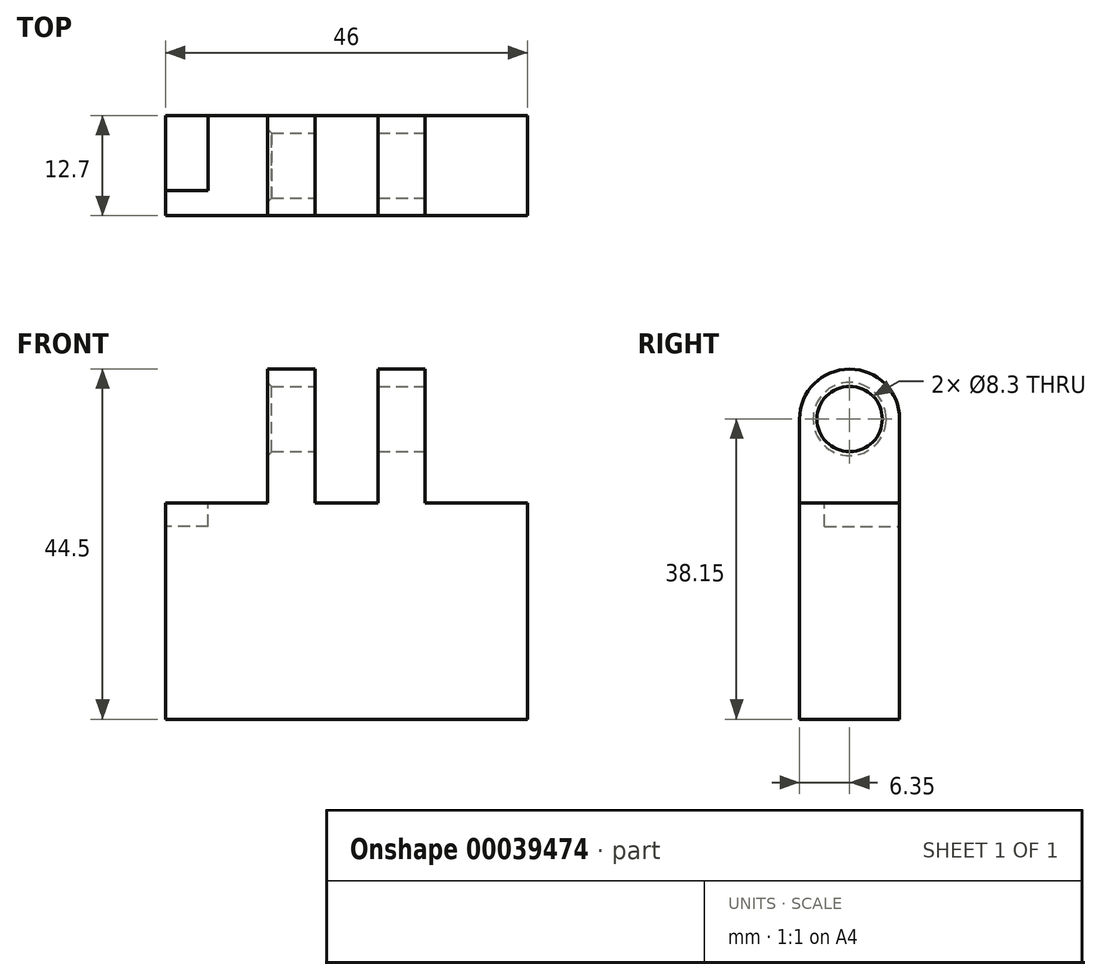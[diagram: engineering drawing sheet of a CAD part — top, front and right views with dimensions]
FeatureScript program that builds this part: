
annotation { "Feature Type Name" : "Feature", "Feature Type Description" : "" }
export const myFeature = defineFeature(function(context is Context, id is Id, definition is map)
    precondition{}
    {
        {
            var Q0;
            Q0=qCreatedBy(makeId("Top.planeOp"),FACE);
            var sketch = newSketch(context, id + "F0", { "sketchPlane" : qUnion([Q0])});
            skLineSegment(sketch, "E0.rect.bottom", {"start": v(23, -6.35) * mm, "end": v(-23, -6.35) * mm});
            skLineSegment(sketch, "E0.rect.top", {"start": v(23, 6.35) * mm, "end": v(-23, 6.35) * mm});
            skLineSegment(sketch, "E0.rect.left", {"start": v(23, -6.35) * mm, "end": v(23, 6.35) * mm});
            skLineSegment(sketch, "E0.rect.right", {"start": v(-23, -6.35) * mm, "end": v(-23, 6.35) * mm});
            skPoint(sketch, "E0.rect.middle", {"position": v(0, 0) * mm});
            skLineSegment(sketch, "E1", {"start": v(-23, 6.35) * mm, "end": v(23, 6.35) * mm});
            skLineSegment(sketch, "E2", {"start": v(-23, -3.2) * mm, "end": v(23, -3.2) * mm});
            skLineSegment(sketch, "E3", {"start": v(-17.6, 6.35) * mm, "end": v(-17.6, -6.35) * mm});
            skLineSegment(sketch, "E4", {"start": v(0, 15.39) * mm, "end": v(0, -22.17) * mm, "construction": true});
            skLineSegment(sketch, "E5.MirrorCS", {"start": v(17.6, 6.35) * mm, "end": v(17.6, -6.35) * mm});
            skLineSegment(sketch, "E6", {"start": v(-31.76, 0) * mm, "end": v(24.03, 0) * mm, "construction": true});
            skSolve(sketch);
        }
        {
            var Q0;
            {var subQ3=sQuery(id+"F0.wireOp",EDGE,"E1");var subQ5=sQuery(id+"F0.wireOp",EDGE,"E0.rect.right");var subQ7=makeQuery(id+"F0.imprint","INTERSECT",VERTEX,{"derivedFrom":[subQ5,subQ3]});Q0=makeQuery(id+"F0.imprint","IMPRINT",FACE,{"disambiguationData":[TD([[makeQuery(id+"F0.imprint","IMPRINT",EDGE,{"disambiguationData":[TD([[subQ7,1.0]])],"derivedFrom":subQ5}),-1.0]])]});}
            var Q1;
            {var subQ3=sQuery(id+"F0.wireOp",EDGE,"E1");var subQ5=sQuery(id+"F0.wireOp",EDGE,"E3");var subQ7=makeQuery(id+"F0.imprint","INTERSECT",VERTEX,{"derivedFrom":[subQ3,subQ5]});Q1=makeQuery(id+"F0.imprint","IMPRINT",FACE,{"disambiguationData":[TD([[makeQuery(id+"F0.imprint","IMPRINT",EDGE,{"disambiguationData":[TD([[subQ7,-1.0]])],"derivedFrom":subQ3}),-1.0]])]});}
            var Q2;
            {var subQ3=sQuery(id+"F0.wireOp",EDGE,"E0.rect.left");var subQ5=sQuery(id+"F0.wireOp",EDGE,"E1");var subQ7=makeQuery(id+"F0.imprint","INTERSECT",VERTEX,{"derivedFrom":[subQ3,subQ5]});Q2=makeQuery(id+"F0.imprint","IMPRINT",FACE,{"disambiguationData":[TD([[makeQuery(id+"F0.imprint","IMPRINT",EDGE,{"disambiguationData":[TD([[subQ7,1.0]])],"derivedFrom":subQ3}),1.0]])]});}
            var Q3;
            {var subQ3=sQuery(id+"F0.wireOp",EDGE,"E0.rect.top");var subQ5=sQuery(id+"F0.wireOp",EDGE,"E0.rect.left");var subQ7=makeQuery(id+"F0.imprint","INTERSECT",VERTEX,{"derivedFrom":[subQ3,subQ5]});Q3=makeQuery(id+"F0.imprint","IMPRINT",FACE,{"disambiguationData":[TD([[makeQuery(id+"F0.imprint","IMPRINT",EDGE,{"disambiguationData":[TD([[subQ7,-1.0]])],"derivedFrom":subQ3}),1.0]])]});}
            var Q4;
            {var subQ0=sQuery(id+"F0.wireOp",EDGE,"E0.rect.left");var subQ3=sQuery(id+"F0.wireOp",EDGE,"E0.rect.bottom");var subQ4=makeQuery(id+"F0.imprint","INTERSECT",VERTEX,{"derivedFrom":[subQ3,subQ0]});Q4=makeQuery(id+"F0.imprint","IMPRINT",FACE,{"disambiguationData":[TD([[makeQuery(id+"F0.imprint","IMPRINT",EDGE,{"disambiguationData":[TD([[subQ4,-1.0]])],"derivedFrom":subQ3}),-1.0]])]});}
            var Q5;
            {var subQ0=sQuery(id+"F0.wireOp",EDGE,"E3");var subQ3=sQuery(id+"F0.wireOp",EDGE,"E0.rect.bottom");var subQ4=makeQuery(id+"F0.imprint","INTERSECT",VERTEX,{"derivedFrom":[subQ3,subQ0]});Q5=makeQuery(id+"F0.imprint","IMPRINT",FACE,{"disambiguationData":[TD([[makeQuery(id+"F0.imprint","IMPRINT",EDGE,{"disambiguationData":[TD([[subQ4,1.0]])],"derivedFrom":subQ3}),-1.0]])]});}
            var Q6;
            {var subQ0=sQuery(id+"F0.wireOp",EDGE,"E3");var subQ3=sQuery(id+"F0.wireOp",EDGE,"E0.rect.top");var subQ4=makeQuery(id+"F0.imprint","INTERSECT",VERTEX,{"derivedFrom":[subQ3,subQ0]});Q6=makeQuery(id+"F0.imprint","IMPRINT",FACE,{"disambiguationData":[TD([[makeQuery(id+"F0.imprint","IMPRINT",EDGE,{"disambiguationData":[TD([[subQ4,1.0]])],"derivedFrom":subQ3}),1.0]])]});}
            var Q7;
            {var subQ3=sQuery(id+"F0.wireOp",EDGE,"E0.rect.top");var subQ5=sQuery(id+"F0.wireOp",EDGE,"E0.rect.right");var subQ7=makeQuery(id+"F0.imprint","INTERSECT",VERTEX,{"derivedFrom":[subQ3,subQ5]});Q7=makeQuery(id+"F0.imprint","IMPRINT",FACE,{"disambiguationData":[TD([[makeQuery(id+"F0.imprint","IMPRINT",EDGE,{"disambiguationData":[TD([[subQ7,1.0]])],"derivedFrom":subQ3}),1.0]])]});}
            var Q8;
            {var subQ3=sQuery(id+"F0.wireOp",EDGE,"E0.rect.bottom");var subQ5=sQuery(id+"F0.wireOp",EDGE,"E0.rect.right");var subQ7=makeQuery(id+"F0.imprint","INTERSECT",VERTEX,{"derivedFrom":[subQ3,subQ5]});Q8=makeQuery(id+"F0.imprint","IMPRINT",FACE,{"disambiguationData":[TD([[makeQuery(id+"F0.imprint","IMPRINT",EDGE,{"disambiguationData":[TD([[subQ7,1.0]])],"derivedFrom":subQ3}),-1.0]])]});}
            extrude(context, id + "F1", {"entities" : qUnion([Q0, Q1, Q2, Q3, Q4, Q5, Q6, Q7, Q8]), "endBound" : BoundingType.SYMMETRIC, "oppositeDirection" : true, "depth" : 24.5 * mm});
        }
        {
            var Q0;
            Q0=makeQuery(id+"F1.opExtrude","CAP_FACE",FACE,{"disambiguationData":[OSD([sQuery(id+"F0.wireOp",EDGE,"E0.rect.bottom"),sQuery(id+"F0.wireOp",EDGE,"E0.rect.top"),sQuery(id+"F0.wireOp",EDGE,"E0.rect.left"),sQuery(id+"F0.wireOp",EDGE,"E0.rect.right"),sQuery(id+"F0.wireOp",EDGE,"E1"),sQuery(id+"F0.wireOp",EDGE,"E2"),sQuery(id+"F0.wireOp",EDGE,"E3"),sQuery(id+"F0.wireOp",EDGE,"E5.MirrorCS"),sQuery(id+"F0.wireOp",EDGE,"1957025f-e252-492f-954e-e706e823597b"),sQuery(id+"F0.wireOp",EDGE,"4d34af1b-1c1c-4e9e-9a2c-87477e56e32b")])],"isStart":true});
            cPlane(context, id + "F2", {"entities" : qUnion([Q0]), "cplaneType" : CPlaneType.OFFSET, "offset" : 5 * mm, "width" : 150 * mm, "height" : 150 * mm});
        }
        {
            var Q0;
            Q0=qCreatedBy(id+"F2.planeOp",FACE);
            var sketch = newSketch(context, id + "F3", { "sketchPlane" : qUnion([Q0])});
            skLineSegment(sketch, "E7.0", {"start": v(-23, -6.35) * mm, "end": v(-23, 6.35) * mm});
            skLineSegment(sketch, "E7.1", {"start": v(23, -6.35) * mm, "end": v(-23, -6.35) * mm});
            skLineSegment(sketch, "E7.2", {"start": v(23, 6.35) * mm, "end": v(-23, 6.35) * mm});
            skLineSegment(sketch, "E7.3", {"start": v(23, -6.35) * mm, "end": v(23, 6.35) * mm});
            skLineSegment(sketch, "E8.0.0", {"start": v(17.6, -3.2) * mm, "end": v(23, -3.2) * mm});
            skLineSegment(sketch, "E8.0.1", {"start": v(23, -3.2) * mm, "end": v(23, 6.35) * mm});
            skLineSegment(sketch, "E8.0.2", {"start": v(23, 6.35) * mm, "end": v(17.6, 6.35) * mm});
            skLineSegment(sketch, "E8.0.3", {"start": v(17.6, 6.35) * mm, "end": v(17.6, -3.2) * mm});
            skLineSegment(sketch, "E8.1.0", {"start": v(-23, 6.35) * mm, "end": v(-23, -3.2) * mm});
            skLineSegment(sketch, "E8.1.1", {"start": v(-23, -3.2) * mm, "end": v(-17.6, -3.2) * mm});
            skLineSegment(sketch, "E8.1.2", {"start": v(-17.6, -3.2) * mm, "end": v(-17.6, 6.35) * mm});
            skLineSegment(sketch, "E8.1.3", {"start": v(-17.6, 6.35) * mm, "end": v(-23, 6.35) * mm});
            skLineSegment(sketch, "E9", {"start": v(4, 6.35) * mm, "end": v(4, -6.35) * mm});
            skLineSegment(sketch, "E10", {"start": v(0, 14.35) * mm, "end": v(0, -25.85) * mm, "construction": true});
            skLineSegment(sketch, "E11.MirrorCS", {"start": v(-4, 6.35) * mm, "end": v(-4, -6.35) * mm});
            skLineSegment(sketch, "E12", {"start": v(10, 6.35) * mm, "end": v(10, -6.35) * mm});
            skLineSegment(sketch, "E13.MirrorCS", {"start": v(-10, 6.35) * mm, "end": v(-10, -6.35) * mm});
            skLineSegment(sketch, "E14", {"start": v(-5.3, -14.65) * mm, "end": v(5.62, -14.65) * mm, "construction": true});
            skArc(sketch, "E15", {"start": v(2.63, -11.1) * mm, "mid": v(0, -12.65) * mm, "end": v(-2.62, -11.1) * mm});
            skLineSegment(sketch, "E16.bottom", {"start": v(-2.5, -14.65) * mm, "end": v(2.5, -14.65) * mm});
            skLineSegment(sketch, "E16.left", {"start": v(-3, -14.15) * mm, "end": v(-3, -11.2) * mm});
            skLineSegment(sketch, "E16.right", {"start": v(3, -14.15) * mm, "end": v(3, -11.2) * mm});
            skPoint(sketch, "E17.visualSharp", {"position": v(-3, -9.65) * mm});
            skArc(sketch, "E17.filletArc", {"start": v(-2.62, -11.1) * mm, "mid": v(-2.85, -11) * mm, "end": v(-3, -11.2) * mm});
            skPoint(sketch, "E18.visualSharp", {"position": v(3, -9.65) * mm});
            skArc(sketch, "E18.filletArc", {"start": v(3, -11.2) * mm, "mid": v(2.85, -11) * mm, "end": v(2.63, -11.1) * mm});
            skPoint(sketch, "E19.visualSharp", {"position": v(-3, -14.65) * mm});
            skArc(sketch, "E19.filletArc", {"start": v(-3, -14.15) * mm, "mid": v(-2.85, -14.5) * mm, "end": v(-2.5, -14.65) * mm});
            skPoint(sketch, "E20.visualSharp", {"position": v(3, -14.65) * mm});
            skArc(sketch, "E20.filletArc", {"start": v(2.5, -14.65) * mm, "mid": v(2.85, -14.5) * mm, "end": v(3, -14.15) * mm});
            skLineSegment(sketch, "E21", {"start": v(-16.67, -25.85) * mm, "end": v(15.57, -25.85) * mm, "construction": true});
            skSolve(sketch);
        }
        {
            var Q0;
            {var subQ0=sQuery(id+"F3.wireOp",EDGE,"E7.1");Q0=makeQuery(id+"F3.imprint","IMPRINT",FACE,{"disambiguationData":[TD([[makeQuery(id+"F3.imprint","IMPRINT",EDGE,{"derivedFrom":subQ0}),-1.0]])]});}
            var Q1;
            Q1=makeQuery(id+"F3.imprint","IMPRINT",FACE,{"disambiguationData":[TD([[makeQuery(id+"F3.imprint","IMPRINT",EDGE,{"derivedFrom":sQuery(id+"F3.wireOp",EDGE,"E8.1.0")}),1.0]])]});
            var Q2;
            Q2=makeQuery(id+"F3.imprint","IMPRINT",FACE,{"disambiguationData":[TD([[makeQuery(id+"F3.imprint","IMPRINT",EDGE,{"derivedFrom":sQuery(id+"F3.wireOp",EDGE,"E8.0.0")}),1.0]])]});
            var Q3;
            {var subQ1=sQuery(id+"F3.wireOp",EDGE,"E8.0.0");Q3=makeQuery(id+"F3.imprint","IMPRINT",FACE,{"disambiguationData":[TD([[makeQuery(id+"F3.imprint","IMPRINT",EDGE,{"derivedFrom":subQ1}),-1.0]])]});}
            var Q4;
            {var subQ1=sQuery(id+"F3.wireOp",EDGE,"E8.1.1");Q4=makeQuery(id+"F3.imprint","IMPRINT",FACE,{"disambiguationData":[TD([[makeQuery(id+"F3.imprint","IMPRINT",EDGE,{"derivedFrom":subQ1}),-1.0]])]});}
            var Q5;
            Q5=makeQuery(id+"F1.opExtrude","CAP_FACE",FACE,{"disambiguationData":[OSD([sQuery(id+"F0.wireOp",EDGE,"E0.rect.bottom"),sQuery(id+"F0.wireOp",EDGE,"E0.rect.top"),sQuery(id+"F0.wireOp",EDGE,"E0.rect.left"),sQuery(id+"F0.wireOp",EDGE,"E0.rect.right"),sQuery(id+"F0.wireOp",EDGE,"E1"),sQuery(id+"F0.wireOp",EDGE,"E2"),sQuery(id+"F0.wireOp",EDGE,"E3"),sQuery(id+"F0.wireOp",EDGE,"E5.MirrorCS"),sQuery(id+"F0.wireOp",EDGE,"1957025f-e252-492f-954e-e706e823597b"),sQuery(id+"F0.wireOp",EDGE,"4d34af1b-1c1c-4e9e-9a2c-87477e56e32b")])],"isStart":true});
            extrude(context, id + "F4", {"entities" : qUnion([Q0, Q1, Q2, Q3, Q4]), "endBound" : BoundingType.UP_TO_SURFACE, "oppositeDirection" : true, "endBoundEntityFace" : qUnion([Q5]), "depth" : 25 * mm, "hasSecondDirection" : true, "secondDirectionOppositeDirection" : true, "secondDirectionDepth" : 2 * mm});
        }
        {
            var Q0;
            Q0=makeQuery(id+"F3.imprint","IMPRINT",FACE,{"disambiguationData":[TD([[makeQuery(id+"F3.imprint","IMPRINT",EDGE,{"derivedFrom":sQuery(id+"F3.wireOp",EDGE,"E8.0.0")}),1.0]])]});
            var Q1;
            Q1=makeQuery(id+"F3.imprint","IMPRINT",FACE,{"disambiguationData":[TD([[makeQuery(id+"F3.imprint","IMPRINT",EDGE,{"derivedFrom":sQuery(id+"F3.wireOp",EDGE,"E8.1.0")}),1.0]])]});
            var Q2;
            Q2=makeQuery(id+"F1.opExtrude","CAP_FACE",FACE,{"disambiguationData":[OSD([sQuery(id+"F0.wireOp",EDGE,"E0.rect.bottom"),sQuery(id+"F0.wireOp",EDGE,"E0.rect.top"),sQuery(id+"F0.wireOp",EDGE,"E0.rect.left"),sQuery(id+"F0.wireOp",EDGE,"E0.rect.right"),sQuery(id+"F0.wireOp",EDGE,"E1"),sQuery(id+"F0.wireOp",EDGE,"E2"),sQuery(id+"F0.wireOp",EDGE,"E3"),sQuery(id+"F0.wireOp",EDGE,"E5.MirrorCS"),sQuery(id+"F0.wireOp",EDGE,"1957025f-e252-492f-954e-e706e823597b"),sQuery(id+"F0.wireOp",EDGE,"4d34af1b-1c1c-4e9e-9a2c-87477e56e32b")])],"isStart":false});
            var Q3;
            Q3=makeQuery(id+"F4.opExtrude","CAP_FACE",FACE,{"disambiguationData":[OSD([sQuery(id+"F3.wireOp",EDGE,"E7.0"),sQuery(id+"F3.wireOp",EDGE,"E7.1"),sQuery(id+"F3.wireOp",EDGE,"E7.2"),sQuery(id+"F3.wireOp",EDGE,"E7.3"),sQuery(id+"F3.wireOp",EDGE,"E8.0.1"),sQuery(id+"F3.wireOp",EDGE,"E8.0.2"),sQuery(id+"F3.wireOp",EDGE,"E8.1.0"),sQuery(id+"F3.wireOp",EDGE,"E8.1.3")])],"isStart":true});
            extrude(context, id + "F5", {"entities" : qUnion([Q0, Q1]), "operationType" : NewBodyOperationType.ADD, "oppositeDirection" : true, "endBoundEntityFace" : qUnion([Q2]), "depth" : 15 * mm, "hasSecondDirection" : true, "secondDirectionBound" : SecondDirectionBoundingType.UP_TO_SURFACE, "secondDirectionOppositeDirection" : true, "secondDirectionBoundEntityFace" : qUnion([Q3]), "secondDirectionDepth" : 10.54 * mm});
        }
        {
            var Q0;
            {var subQ2=sQuery(id+"F3.wireOp",EDGE,"E9");Q0=makeQuery(id+"F3.imprint","IMPRINT",FACE,{"disambiguationData":[TD([[makeQuery(id+"F3.imprint","IMPRINT",EDGE,{"derivedFrom":subQ2}),1.0]])]});}
            var Q1;
            {var subQ1=sQuery(id+"F3.wireOp",EDGE,"E11.MirrorCS");Q1=makeQuery(id+"F3.imprint","IMPRINT",FACE,{"disambiguationData":[TD([[makeQuery(id+"F3.imprint","IMPRINT",EDGE,{"derivedFrom":subQ1}),-1.0]])]});}
            var Q2;
            Q2=makeQuery(id+"F4.opExtrude","CAP_FACE",FACE,{"disambiguationData":[OSD([sQuery(id+"F3.wireOp",EDGE,"E7.0"),sQuery(id+"F3.wireOp",EDGE,"E7.1"),sQuery(id+"F3.wireOp",EDGE,"E7.2"),sQuery(id+"F3.wireOp",EDGE,"E7.3"),sQuery(id+"F3.wireOp",EDGE,"E8.0.1"),sQuery(id+"F3.wireOp",EDGE,"E8.0.2"),sQuery(id+"F3.wireOp",EDGE,"E8.1.0"),sQuery(id+"F3.wireOp",EDGE,"E8.1.3")])],"isStart":true});
            extrude(context, id + "F6", {"entities" : qUnion([Q0, Q1]), "operationType" : NewBodyOperationType.ADD, "depth" : 15 * mm, "hasSecondDirection" : true, "secondDirectionBound" : SecondDirectionBoundingType.UP_TO_SURFACE, "secondDirectionOppositeDirection" : true, "secondDirectionBoundEntityFace" : qUnion([Q2]), "secondDirectionDepth" : 25 * mm});
        }
        {
            var Q0;
            Q0=makeQuery(id+"F6.opExtrude","SWEPT_FACE",FACE,{"disambiguationData":[OSD([sQuery(id+"F3.wireOp",EDGE,"E12")])]});
            var sketch = newSketch(context, id + "F7", { "sketchPlane" : qUnion([Q0])});
            skLineSegment(sketch, "E22.bottom", {"start": v(-6.35, 32.25) * mm, "end": v(6.35, 32.25) * mm});
            skLineSegment(sketch, "E22.top", {"start": v(-6.35, 19.55) * mm, "end": v(6.35, 19.55) * mm});
            skLineSegment(sketch, "E22.left", {"start": v(-6.35, 32.25) * mm, "end": v(-6.35, 19.55) * mm});
            skLineSegment(sketch, "E22.right", {"start": v(6.35, 32.25) * mm, "end": v(6.35, 19.55) * mm});
            skLineSegment(sketch, "E23", {"start": v(-6.35, 32.25) * mm, "end": v(6.35, 19.55) * mm, "construction": true});
            skLineSegment(sketch, "E24", {"start": v(-6.35, 19.55) * mm, "end": v(6.35, 32.25) * mm, "construction": true});
            skCircle(sketch, "E25", {"center": v(0, 25.9) * mm, "radius": 4.15 * mm});
            skCircle(sketch, "E26", {"center": v(0, 25.9) * mm, "radius": 11 * mm});
            skLineSegment(sketch, "E27.0", {"start": v(-3.2, 2.25) * mm, "end": v(6.35, 2.25) * mm});
            skSolve(sketch);
        }
        {
            var Q0;
            Q0=makeQuery(id+"F7.imprint","IMPRINT",FACE,{"disambiguationData":[TD([[makeQuery(id+"F7.imprint","IMPRINT",EDGE,{"derivedFrom":sQuery(id+"F7.wireOp",EDGE,"E25")}),1.0]])]});
            extrude(context, id + "F8", {"entities" : qUnion([Q0]), "operationType" : NewBodyOperationType.REMOVE, "oppositeDirection" : true, "depth" : 25 * mm});
        }
        {
            var Q0;
            {var subQ0=sQuery(id+"F3.wireOp",EDGE,"E7.2");Q0=makeQuery(id+"F6.opExtrude","CAP_EDGE",EDGE,{"disambiguationData":[OSD([subQ0]),TDD([makeQuery(id+"F3.imprint","IMPRINT",EDGE,{"disambiguationData":[TD([[makeQuery(id+"F3.imprint","INTERSECT",VERTEX,{"derivedFrom":[subQ0,sQuery(id+"F3.wireOp",EDGE,"E11.MirrorCS")]}),-1.0]])],"derivedFrom":subQ0})])],"isStart":false});}
            var Q1;
            {var subQ0=sQuery(id+"F3.wireOp",EDGE,"E7.2");Q1=makeQuery(id+"F6.opExtrude","CAP_EDGE",EDGE,{"disambiguationData":[OSD([subQ0]),TDD([makeQuery(id+"F3.imprint","IMPRINT",EDGE,{"disambiguationData":[TD([[makeQuery(id+"F3.imprint","INTERSECT",VERTEX,{"derivedFrom":[subQ0,sQuery(id+"F3.wireOp",EDGE,"E9")]}),1.0]])],"derivedFrom":subQ0})])],"isStart":false});}
            var Q2;
            {var subQ0=sQuery(id+"F3.wireOp",EDGE,"E7.1");Q2=makeQuery(id+"F6.opExtrude","CAP_EDGE",EDGE,{"disambiguationData":[OSD([subQ0]),TDD([makeQuery(id+"F3.imprint","IMPRINT",EDGE,{"disambiguationData":[TD([[makeQuery(id+"F3.imprint","INTERSECT",VERTEX,{"derivedFrom":[subQ0,sQuery(id+"F3.wireOp",EDGE,"E11.MirrorCS")]}),-1.0]])],"derivedFrom":subQ0})])],"isStart":false});}
            var Q3;
            {var subQ0=sQuery(id+"F3.wireOp",EDGE,"E7.1");Q3=makeQuery(id+"F6.opExtrude","CAP_EDGE",EDGE,{"disambiguationData":[OSD([subQ0]),TDD([makeQuery(id+"F3.imprint","IMPRINT",EDGE,{"disambiguationData":[TD([[makeQuery(id+"F3.imprint","INTERSECT",VERTEX,{"derivedFrom":[subQ0,sQuery(id+"F3.wireOp",EDGE,"E9")]}),1.0]])],"derivedFrom":subQ0})])],"isStart":false});}
            fillet(context, id + "F9", {"entities" : qUnion([Q0, Q1, Q2, Q3]), "radius" : 6.35 * mm, "tangentPropagation" : true, "allowEdgeOverflow" : false});
        }
        {
            var Q0;
            Q0=makeQuery(id+"F8.boolean.opBoolean","INTERSECT",EDGE,{"derivedFrom":[makeQuery(id+"F6.opExtrude","SWEPT_FACE",FACE,{"disambiguationData":[OSD([sQuery(id+"F3.wireOp",EDGE,"E13.MirrorCS")])]}),makeQuery(id+"F8.opExtrude","SWEPT_FACE",FACE,{"disambiguationData":[OSD([sQuery(id+"F7.wireOp",EDGE,"E25")])]})]});
            var Q1;
            Q1=makeQuery(id+"F8.boolean.opBoolean","COPY",EDGE,{"derivedFrom":makeQuery(id+"F8.opExtrude","CAP_EDGE",EDGE,{"disambiguationData":[OSD([sQuery(id+"F7.wireOp",EDGE,"E25")])],"isStart":true})});
            chamfer(context, id + "F10", {"entities" : qUnion([Q0, Q1]), "width" : .5 * mm, "tangentPropagation" : true});
        }
    });
